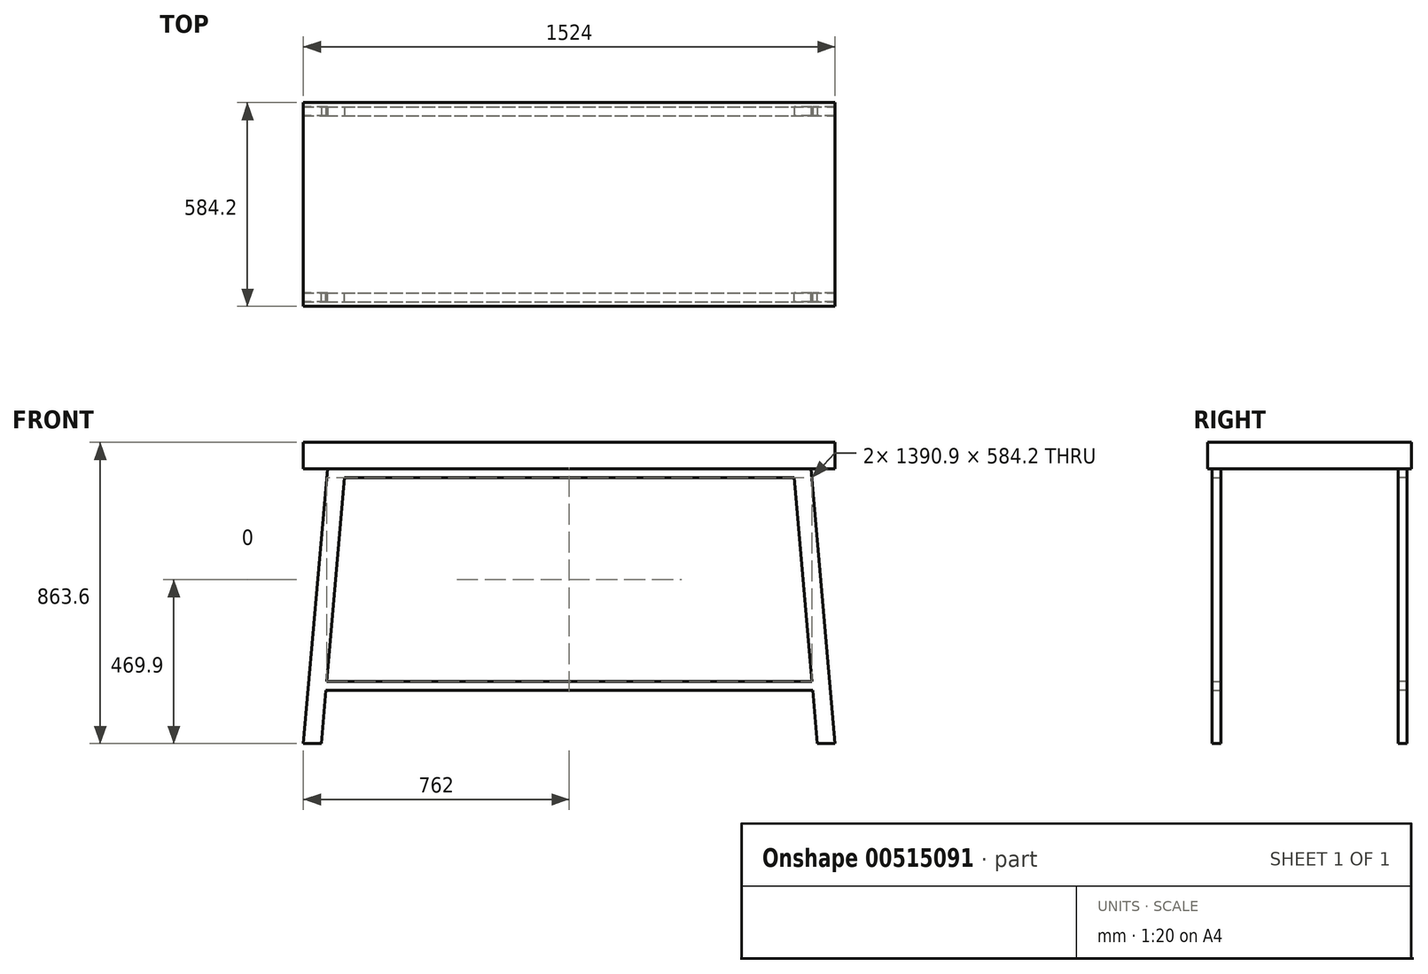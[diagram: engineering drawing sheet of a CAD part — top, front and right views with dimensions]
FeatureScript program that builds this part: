
annotation { "Feature Type Name" : "Feature", "Feature Type Description" : "" }
export const myFeature = defineFeature(function(context is Context, id is Id, definition is map)
    precondition{}
    {
        {
            var Q0;
            Q0=qCreatedBy(makeId("Top.planeOp"),FACE);
            var sketch = newSketch(context, id + "F0", { "sketchPlane" : qUnion([Q0])});
            skLineSegment(sketch, "E0.bottom", {"start": v(-762, 292.1) * mm, "end": v(762, 292.1) * mm});
            skLineSegment(sketch, "E0.top", {"start": v(-762, -292.1) * mm, "end": v(762, -292.1) * mm});
            skLineSegment(sketch, "E0.left", {"start": v(-762, 292.1) * mm, "end": v(-762, -292.1) * mm});
            skLineSegment(sketch, "E0.right", {"start": v(762, 292.1) * mm, "end": v(762, -292.1) * mm});
            skLineSegment(sketch, "E1", {"start": v(0, 292.1) * mm, "end": v(0, -292.1) * mm, "construction": true});
            skPoint(sketch, "E2.endSnap0", {"position": v(-762, 0) * mm});
            skLineSegment(sketch, "E3", {"start": v(762, 0) * mm, "end": v(-762, 0) * mm, "construction": true});
            skSolve(sketch);
        }
        {
            var Q0;
            Q0 = qSketchRegion(id + "F0", true);
            extrude(context, id + "F1", {"entities" : qUnion([Q0]), "depth" : 76.2 * mm, "offsetDistance" : 25.4 * mm});
        }
        {
            var Q0;
            Q0=makeQuery(id+"F1.opExtrude","CAP_FACE",FACE,{"disambiguationData":[OSD([sQuery(id+"F0.wireOp",EDGE,"E0.bottom"),sQuery(id+"F0.wireOp",EDGE,"E0.top"),sQuery(id+"F0.wireOp",EDGE,"E0.left"),sQuery(id+"F0.wireOp",EDGE,"E0.right")])],"isStart":false});
            cPlane(context, id + "F2", {"entities" : qUnion([Q0]), "cplaneType" : CPlaneType.OFFSET, "offset" : 863.6 * mm, "oppositeDirection" : true, "width" : 152.4 * mm, "height" : 152.4 * mm});
        }
        {
            var Q0;
            Q0=qCreatedBy(makeId("Front.planeOp"),FACE);
            cPlane(context, id + "F3", {"entities" : qUnion([Q0]), "cplaneType" : CPlaneType.OFFSET, "offset" : 254 * mm, "width" : 152.4 * mm, "height" : 152.4 * mm});
        }
        {
            var Q0;
            Q0=qCreatedBy(id+"F3.planeOp",FACE);
            var sketch = newSketch(context, id + "F4", { "sketchPlane" : qUnion([Q0])});
            skLineSegment(sketch, "E4.0", {"start": v(-762, 0) * mm, "end": v(642.12, 0) * mm, "construction": true});
            skLineSegment(sketch, "E5", {"start": v(-693.11, 0) * mm, "end": v(-762, -787.4) * mm});
            skLineSegment(sketch, "E6", {"start": v(-762, -787.4) * mm, "end": v(-711, -787.4) * mm});
            skLineSegment(sketch, "E7", {"start": v(-711, -787.4) * mm, "end": v(-644.34, -25.4) * mm});
            skLineSegment(sketch, "E8", {"start": v(-664.83, -259.6) * mm, "end": v(-715.44, -255.17) * mm, "construction": true});
            skLineSegment(sketch, "E9", {"start": v(-762, -787.4) * mm, "end": v(-762, 0) * mm, "construction": true});
            skLineSegment(sketch, "E10.MirrorCS", {"start": v(711, -787.4) * mm, "end": v(644.34, -25.4) * mm});
            skLineSegment(sketch, "E11.MirrorCS", {"start": v(693.11, 0) * mm, "end": v(762, -787.4) * mm});
            skLineSegment(sketch, "E12.MirrorCS", {"start": v(762, -787.4) * mm, "end": v(711, -787.4) * mm});
            skLineSegment(sketch, "E13.bottom", {"start": v(-693.11, 0) * mm, "end": v(693.11, 0) * mm});
            skLineSegment(sketch, "E13.top", {"start": v(-695.33, -25.4) * mm, "end": v(695.33, -25.4) * mm});
            skLineSegment(sketch, "E14.trimOffspring", {"start": v(695.33, 0) * mm, "end": v(762, 0) * mm, "construction": true});
            skLineSegment(sketch, "E15.bottom", {"start": v(-697.67, -635) * mm, "end": v(697.67, -635) * mm});
            skLineSegment(sketch, "E15.top", {"start": v(-695.45, -609.6) * mm, "end": v(695.45, -609.6) * mm});
            skSolve(sketch);
        }
        {
            var Q0;
            {var subQ3=sQuery(id+"F4.wireOp",EDGE,"E6");Q0=makeQuery(id+"F4.imprint","IMPRINT",FACE,{"disambiguationData":[TD([[makeQuery(id+"F4.imprint","IMPRINT",EDGE,{"derivedFrom":subQ3}),1.0]])]});}
            var Q1;
            {var subQ0=sQuery(id+"F4.wireOp",EDGE,"E12.MirrorCS");Q1=makeQuery(id+"F4.imprint","IMPRINT",FACE,{"disambiguationData":[TD([[makeQuery(id+"F4.imprint","IMPRINT",EDGE,{"derivedFrom":subQ0}),-1.0]])]});}
            var Q2;
            {var subQ4=sQuery(id+"F4.wireOp",EDGE,"E13.bottom");Q2=makeQuery(id+"F4.imprint","IMPRINT",FACE,{"disambiguationData":[TD([[makeQuery(id+"F4.imprint","IMPRINT",EDGE,{"derivedFrom":subQ4}),-1.0]])]});}
            var Q3;
            {var subQ0=sQuery(id+"F4.wireOp",EDGE,"E15.bottom");Q3=makeQuery(id+"F4.imprint","IMPRINT",FACE,{"disambiguationData":[TD([[makeQuery(id+"F4.imprint","IMPRINT",EDGE,{"derivedFrom":subQ0}),1.0]])]});}
            extrude(context, id + "F5", {"entities" : qUnion([Q0, Q1, Q2, Q3]), "operationType" : NewBodyOperationType.ADD, "depth" : 25.4 * mm, "offsetDistance" : 25.4 * mm});
        }
        {
            var Q0;
            Q0=makeQuery(id+"F1.opExtrude","SWEPT_BODY",BODY,{"disambiguationData":[OSD([sQuery(id+"F0.wireOp",EDGE,"E0.bottom"),sQuery(id+"F0.wireOp",EDGE,"E0.top"),sQuery(id+"F0.wireOp",EDGE,"E0.left"),sQuery(id+"F0.wireOp",EDGE,"E0.right")])]});
            var Q1;
            Q1=qCreatedBy(makeId("Front.planeOp"),FACE);
            mirror(context, id + "F6", {"operationType" : NewBodyOperationType.ADD, "entities" : qUnion([Q0]), "mirrorPlane" : qUnion([Q1])});
        }
    });
